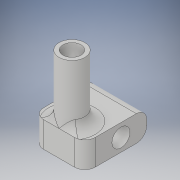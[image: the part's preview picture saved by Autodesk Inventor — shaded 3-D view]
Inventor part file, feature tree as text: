
AUTODESK INVENTOR PART (.ipt)
format: ipt  version: 2019.4 (Build 234330000, 330)  size: 178,688 bytes
history: native  units: mm
features: extrude x4, sketch x4, fillet x2, plane x1
ambient origin geometry x8: Origin, YZ Plane, XZ Plane, XY Plane, X Axis, Y Axis, Z Axis, Center Point
bodies: Solid1 (feature_tree)
feature tree (11):
  extrude  "Extrusion1"  Depth=5.0mm
  plane  "Work Plane1"
  extrude  "Extrusion2"  Depth=2.5mm
  extrude  "Extrusion3"  TaperAngle=90.0deg  [1 undecoded]
  fillet  "Fillet1"  Radius=10.0mm
  fillet  "Fillet2"  Radius=5.0mm
  extrude  "Extrusion4"  Depth=2.0mm
  sketch  "Sketch1"  dims[d0=3.5mm d1=5.0mm]
  sketch  "Sketch3"  dims[d2=13.0mm d3=0.0mm d7=2.5mm]
  sketch  "Sketch4"  dims[d8=14.45mm d9=90.0deg d10=10.0mm d11=5.0mm]
  sketch  "Sketch5"  dims[d12=12.0mm d13=0.0mm d14=5.0mm d15=3.5mm d16=12.0mm d17=0.0mm d18=2.0mm d19=2.0mm d20=3.5mm d21=26.0mm d22=0.0mm]
note: 1 required parameter value undecoded (feature->parameter linkage not recoverable at this tier; creation-order binding heuristic only, values carry confidence <= 0.55)
